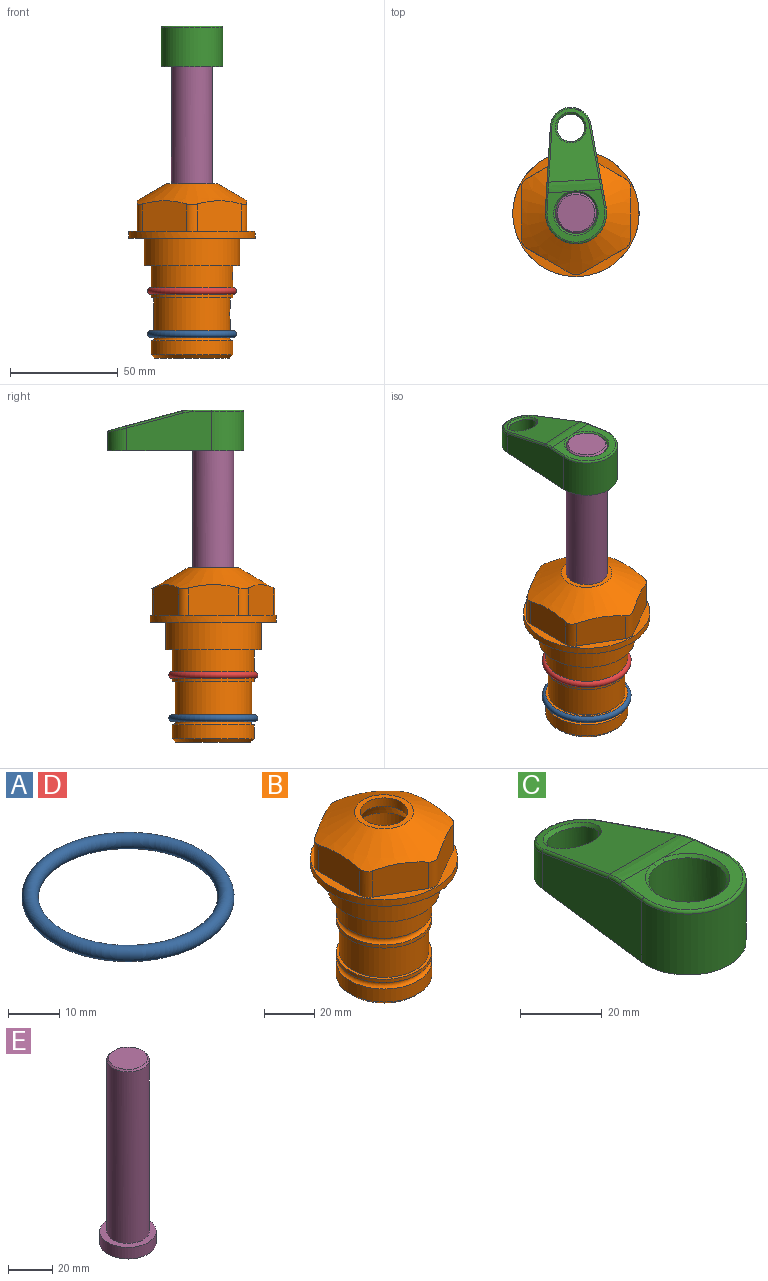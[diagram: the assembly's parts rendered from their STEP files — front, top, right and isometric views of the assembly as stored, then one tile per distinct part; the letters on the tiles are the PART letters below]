
ASSEMBLY  parts=5 mates=4
PART A: 1 faces, bbox 44.7x44.7x3.2 mm
  f0: torus R=19.05mm, axis (0,0,1), area 1193.9mm2
PART B: 36 faces, bbox 58.7x58.7x81 mm
  f0: cylinder r=17.78mm len=35.56mm, axis (0,0,1), area 1670.8mm2, adj f23,f24,f31
  f1: cylinder r=19.05mm len=38.1mm, axis (0,0,1), area 1191.9mm2, adj f26,f27,f30
  f2: plane 58.66x58.66mm, normal (0,0,-1), area 1150.6mm2, adj f3,f28
  f3: cylinder r=29.33mm len=58.66mm, axis (0,0,-1), area 585.1mm2, adj f2,f4
  f4: plane 58.66x58.66mm, normal (0,0,1), area 475.9mm2, adj f3,f5,f6,f7,f8,f9,f10,f11
  f5: plane 20.32x14.34mm, normal (-0.5,0.87,0), area 324.4mm2, adj f4,f15,f16,f17
  f6: plane 20.32x14.34mm, normal (0.5,0.87,0), area 324.4mm2, adj f4,f14,f15,f17
  f7: plane 23.48x14.34mm, normal (1,0,0), area 324.4mm2, adj f4,f13,f14,f17
  f8: plane 20.32x14.34mm, normal (0.5,-0.87,0), area 324.4mm2, adj f4,f12,f13,f17
  f9: plane 20.32x14.34mm, normal (-0.5,-0.87,0), area 324.4mm2, adj f4,f11,f12,f17
  f10: plane 23.48x14.34mm, normal (-1,0,0), area 324.4mm2, adj f4,f11,f16,f17
  f11: cylinder r=5.08mm len=12.85mm, axis (0,0,-1), area 67.2mm2, adj f4,f9,f10,f17
  f12: cylinder r=5.08mm len=12.85mm, axis (0,0,-1), area 67.2mm2, adj f4,f8,f9,f17
  f13: cylinder r=5.08mm len=12.85mm, axis (0,0,-1), area 67.2mm2, adj f4,f7,f8,f17
  f14: cylinder r=5.08mm len=12.85mm, axis (0,0,-1), area 67.2mm2, adj f4,f6,f7,f17
  f15: cylinder r=5.08mm len=12.85mm, axis (0,0,-1), area 67.2mm2, adj f4,f5,f6,f17
  f16: cylinder r=5.08mm len=12.85mm, axis (0,0,-1), area 67.2mm2, adj f4,f5,f10,f17
  f17: cone r=11.73mm half-angle=60deg, axis (0,0,-1), area 2071.8mm2, adj f5,f6,f7,f8,f9,f10,f11,f12
  f18: plane 23.46x23.46mm, normal (0,0,1), area 147.4mm2, adj f17,f35
  f19: plane 34.93x34.93mm, normal (0,0,-1), area 958mm2, adj f29
  f20: cylinder r=19.05mm len=38.1mm, axis (0,0,1), area 760.1mm2, adj f21,f29
  f21: torus R=19.05mm, axis (0,0,1), area 565.3mm2, adj f20,f22
  f22: cylinder r=19.05mm len=38.1mm, axis (0,0,1), area 190mm2, adj f21,f23
  f23: plane 38.1x38.1mm, normal (0,0,1), area 146.9mm2, adj f0,f22
  f24: plane 38.1x38.1mm, normal (0,0,-1), area 146.9mm2, adj f0,f25
  f25: cylinder r=19.05mm len=38.1mm, axis (0,0,1), area 190mm2, adj f24,f26
  f26: torus R=19.05mm, axis (0,0,1), area 565.3mm2, adj f1,f25
  f27: plane 44.45x44.45mm, normal (0,0,-1), area 411.7mm2, adj f1,f28
  f28: cylinder r=22.23mm len=44.45mm, axis (0,0,1), area 1773.5mm2, adj f2,f27
  f29: cone r=19.05mm half-angle=45deg, axis (0,0,1), area 257.5mm2, adj f19,f20
  f30: cylinder r=3.17mm len=6.75mm, axis (-1,0,0), area 128mm2, adj f1,f33
  f31: cylinder r=3.17mm len=6.35mm, axis (-1,0,0), area 102.5mm2, adj f0,f33
  f32: plane 25.4x25.4mm, normal (0,0,1), area 506.7mm2, adj f33
  f33: cylinder r=12.7mm len=66.42mm, axis (0,0,-1), area 5236.2mm2, adj f30,f31,f32,f34
  f34: cone r=9.53mm half-angle=30deg, axis (0,0,-1), area 443.4mm2, adj f33,f35
  f35: cylinder r=9.53mm len=19.05mm, axis (0,0,-1), area 240.9mm2, adj f18,f34
PART C: 31 faces, bbox 31.7x65.5x19.8 mm
  f0: plane 39.12x18.26mm, normal (0.99,0.12,0), area 612.2mm2, adj f1,f4,f7,f11,f13,f15
  f1: cylinder r=9.53mm len=18.91mm, axis (0,0,-1), area 296.1mm2, adj f0,f2,f7,f17
  f2: plane 39.12x18.26mm, normal (-0.99,0.12,0), area 612.2mm2, adj f1,f4,f7,f12,f14,f16
  f3: cylinder r=6.35mm len=12.7mm, axis (0,0,-1), area 362.4mm2, adj f7,f18
  f4: cylinder r=14.29mm len=28.58mm, axis (0,0,-1), area 882.2mm2, adj f0,f2,f7,f10
  f5: cylinder r=9.53mm len=19.05mm, axis (0,0,-1), area 1092.6mm2, adj f7,f19,f20
  f6: plane 26.99x23.69mm, normal (0,0,1), area 216.2mm2, adj f9,f10,f11,f12,f19
  f7: plane 63.5x28.58mm, normal (0,0,-1), area 661.8mm2, adj f0,f1,f2,f3,f4,f5,f22,f23
  f8: plane 33.52x23.6mm, normal (0,0.26,0.97), area 486mm2, adj f9,f15,f16,f17,f18
  f9: cylinder r=19.05mm len=24.72mm, axis (1,0,0), area 120.4mm2, adj f6,f8,f13,f14,f20
  f10: torus R=13.49mm, axis (0,0,1), area 59mm2, adj f4,f6,f11,f12
  f11: cylinder r=0.79mm len=8.67mm, axis (0.12,-0.99,0), area 10.8mm2, adj f0,f6,f10,f13
  f12: cylinder r=0.79mm len=8.67mm, axis (0.12,0.99,0), area 10.8mm2, adj f2,f6,f10,f14
  f13: bspline ~4.95x1.42mm, area 6.1mm2, adj f0,f9,f11,f15
  f14: bspline ~4.95x1.42mm, area 6.1mm2, adj f2,f9,f12,f16
  f15: cylinder r=0.79mm len=25.95mm, axis (0.12,-0.96,0.26), area 32.9mm2, adj f0,f8,f13,f17
  f16: cylinder r=0.79mm len=25.95mm, axis (0.12,0.96,-0.26), area 32.9mm2, adj f2,f8,f14,f17
  f17: bspline ~18.91x8.38mm, area 30mm2, adj f1,f8,f15,f16
  f18: bspline ~14.29x14.29mm, area 48.3mm2, adj f3,f8
  f19: cone r=9.53mm half-angle=45deg, axis (0,0,1), area 66.5mm2, adj f5,f6,f20
  f20: bspline ~3.22x0.96mm, area 3.5mm2, adj f5,f9,f19
  f21: plane 2.75x2.72mm, normal (0,0,-1), area 2.9mm2, adj f23,f25,f28
  f22: plane 23.05x15.88mm, normal (-0.99,-0.12,0), area 323.6mm2, adj f7,f25,f26,f27,f28,f29
  f23: plane 23.05x15.88mm, normal (0.99,-0.12,0), area 323.6mm2, adj f7,f21,f25,f27,f28,f30
  f24: cylinder r=9.53mm len=10.69mm, axis (0,0,-1), area 114.7mm2, adj f7,f27,f29,f30
  f25: cylinder r=12.7mm len=20.59mm, axis (0,0,-1), area 381.1mm2, adj f7,f21,f22,f23,f26,f28
  f26: plane 2.75x2.72mm, normal (0,0,-1), area 2.9mm2, adj f22,f25,f28
  f27: plane 19.72x18.37mm, normal (0,-0.26,-0.97), area 291.8mm2, adj f22,f23,f24,f28,f29,f30
  f28: cylinder r=15.88mm len=19.92mm, axis (1,0,0), area 54.8mm2, adj f21,f22,f23,f25,f26,f27
  f29: cylinder r=1.59mm len=11mm, axis (0,0,-1), area 34.7mm2, adj f7,f22,f24,f27
  f30: cylinder r=1.59mm len=11mm, axis (0,0,-1), area 34.7mm2, adj f7,f23,f24,f27
PART D: same geometry as A
PART E: 6 faces, bbox 25.4x25.4x101.6 mm
  f0: plane 17.46x17.46mm, normal (0,0,1), area 239.5mm2, adj f5
  f1: plane 25.4x25.4mm, normal (0,0,-1), area 506.7mm2, adj f2
  f2: cylinder r=12.7mm len=25.4mm, axis (0,0,1), area 506.7mm2, adj f1,f3
  f3: plane 25.4x25.4mm, normal (0,0,1), area 221.7mm2, adj f2,f4
  f4: cylinder r=9.53mm len=94.46mm, axis (0,0,1), area 5653mm2, adj f3,f5
  f5: cone r=8.73mm half-angle=45deg, axis (0,0,-1), area 64.4mm2, adj f0,f4
PLACE A t=(0,0,-20)mm
PLACE B at identity fixed
PLACE C rot(axis=(0,0,1),3.5deg) t=(0,0,35.17)mm
PLACE D at identity
PLACE E rot(axis=(0,0,1),3.5deg) t=(0,0,35.17)mm
MATE fastened A.f0 <-> B.f0  axis (0,0,1) through (0,0,-44.51)mm
MATE fastened D.f0 <-> B.f0  axis (0,0,1) through (0,0,-24.51)mm
MATE cylindrical E.f2 <-> B.f0  axis (0,0,-1) through (0,0,-2.93)mm
MATE fastened E.f2 <-> C.f4  axis (0,0,1) through (0,0,98.67)mm
